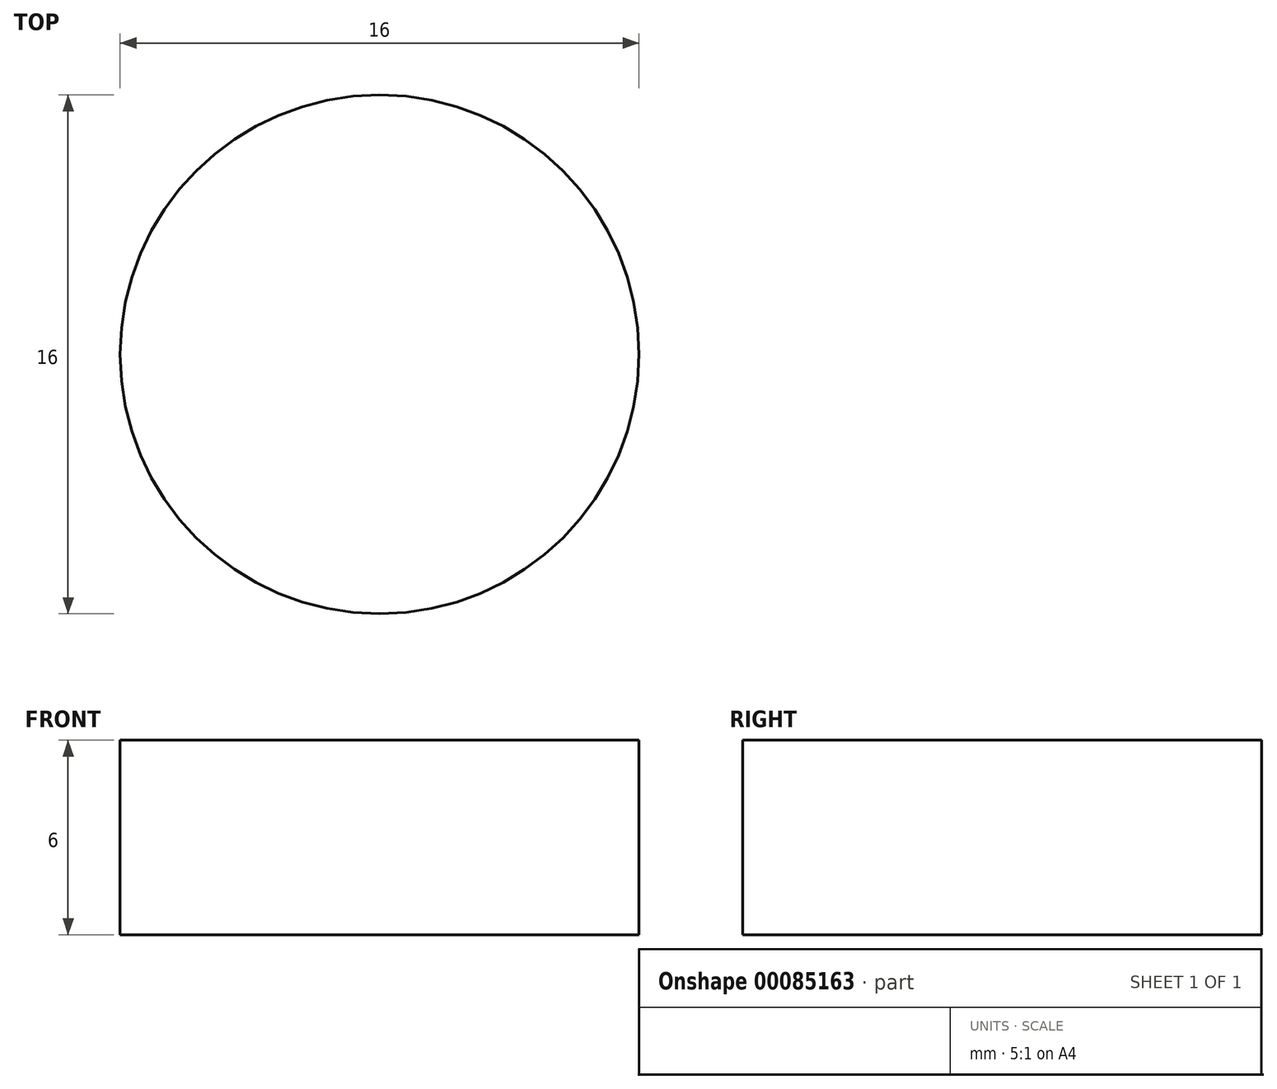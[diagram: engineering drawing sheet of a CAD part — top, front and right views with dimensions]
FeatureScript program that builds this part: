
annotation { "Feature Type Name" : "Feature", "Feature Type Description" : "" }
export const myFeature = defineFeature(function(context is Context, id is Id, definition is map)
    precondition{}
    {
        {
            var Q0;
            Q0=qCreatedBy(makeId("Top.planeOp"),FACE);
            var sketch = newSketch(context, id + "F0", { "sketchPlane" : qUnion([Q0])});
            skLineSegment(sketch, "E0", {"start": v(0, 0) * mm, "end": v(8, 0) * mm});
            skCircle(sketch, "E1", {"center": v(0, 0) * mm, "radius": 8 * mm});
            skSolve(sketch);
        }
        {
            var Q0;
            Q0=makeQuery(id+"F0.imprint","IMPRINT",FACE,{"disambiguationData":[TD([[makeQuery(id+"F0.imprint","IMPRINT",EDGE,{"derivedFrom":sQuery(id+"F0.wireOp",EDGE,"E1")}),1.0]])]});
            extrude(context, id + "F1", {"entities" : qUnion([Q0]), "depth" : 6 * mm});
        }
    });
